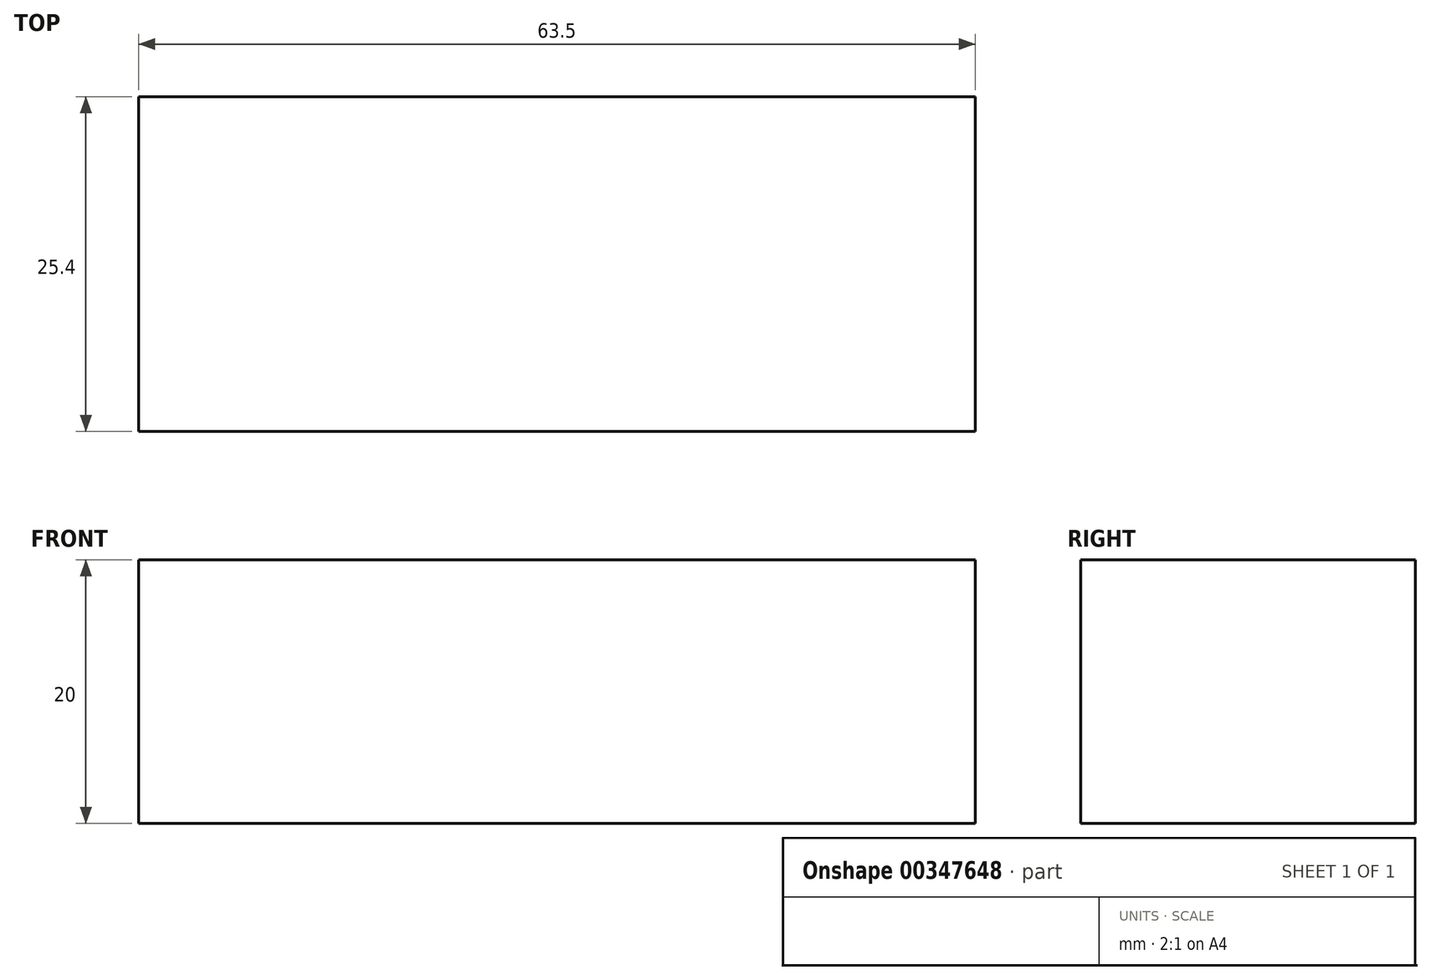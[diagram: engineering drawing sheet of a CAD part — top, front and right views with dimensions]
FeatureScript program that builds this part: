
annotation { "Feature Type Name" : "Feature", "Feature Type Description" : "" }
export const myFeature = defineFeature(function(context is Context, id is Id, definition is map)
    precondition{}
    {
        {
            var Q0;
            Q0=qCreatedBy(makeId("Top.planeOp"),FACE);
            var sketch = newSketch(context, id + "F0", { "sketchPlane" : qUnion([Q0])});
            skLineSegment(sketch, "E0.bottom", {"start": v(0, 0) * mm, "end": v(-63.5, 0) * mm});
            skLineSegment(sketch, "E0.top", {"start": v(0, 25.4) * mm, "end": v(-63.5, 25.4) * mm});
            skLineSegment(sketch, "E0.left", {"start": v(0, 0) * mm, "end": v(0, 25.4) * mm});
            skLineSegment(sketch, "E0.right", {"start": v(-63.5, 0) * mm, "end": v(-63.5, 25.4) * mm});
            skSolve(sketch);
        }
        {
            var Q0;
            Q0=makeQuery(id+"F0.imprint","IMPRINT",FACE,{"disambiguationData":[TD([[makeQuery(id+"F0.imprint","IMPRINT",EDGE,{"derivedFrom":sQuery(id+"F0.wireOp",EDGE,"E0.bottom")}),-1.0]])]});
            extrude(context, id + "F1", {"entities" : qUnion([Q0]), "depth" : 20 * mm});
        }
    });
